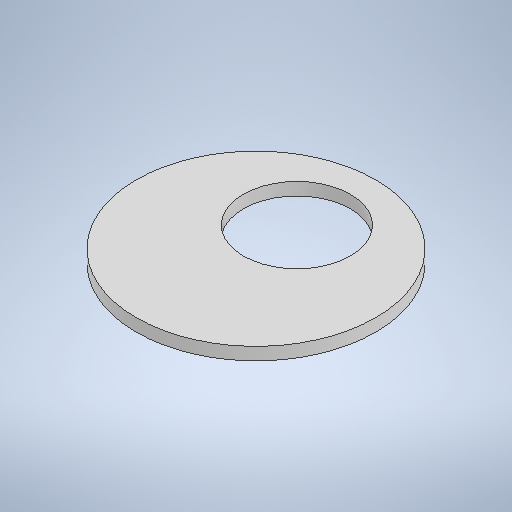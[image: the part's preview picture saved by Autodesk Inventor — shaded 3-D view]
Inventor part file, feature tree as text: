
AUTODESK INVENTOR PART (.ipt)
format: ipt  version: 2025.1 (Build 291241000, 241)  size: 235,008 bytes
history: native  units: mm
features: extrude x1, sketch x1
ambient origin geometry x8: Origin, YZ Plane, XZ Plane, XY Plane, X Axis, Y Axis, Z Axis, Center Point
bodies: Solid1 (feature_tree)
feature tree (2):
  extrude  "Extrusion1"  Depth=3.25mm
  sketch  "Sketch1"  dims[d0=19.0mm d1=3.25mm d2=8.5mm d3=1.0mm d4=0.0mm]
